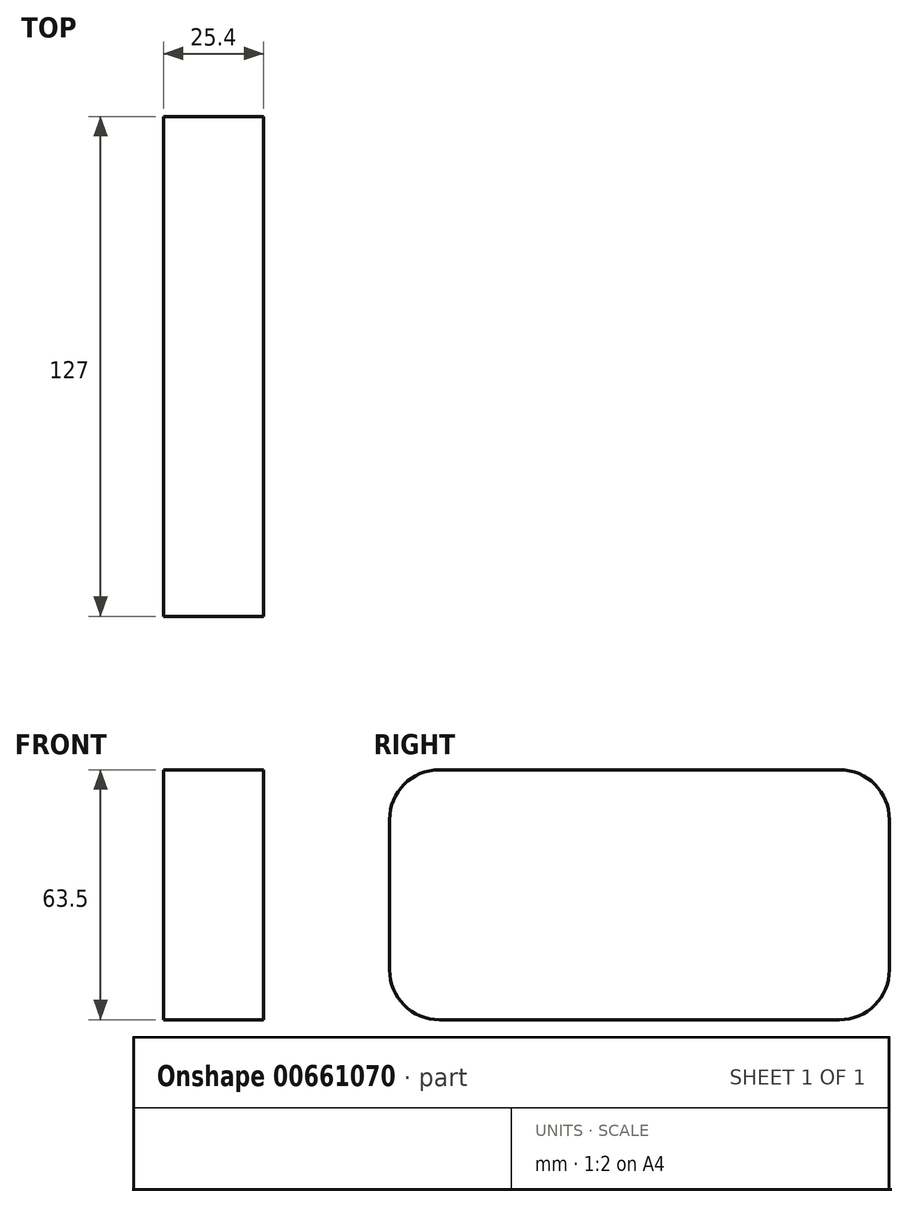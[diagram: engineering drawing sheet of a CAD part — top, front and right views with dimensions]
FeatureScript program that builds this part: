
annotation { "Feature Type Name" : "Feature", "Feature Type Description" : "" }
export const myFeature = defineFeature(function(context is Context, id is Id, definition is map)
    precondition{}
    {
        {
            var Q0;
            Q0=qCreatedBy(makeId("Right.planeOp"),FACE);
            var sketch = newSketch(context, id + "F0", { "sketchPlane" : qUnion([Q0])});
            skLineSegment(sketch, "E0.bottom", {"start": v(50.8, 31.75) * mm, "end": v(-50.8, 31.75) * mm});
            skLineSegment(sketch, "E0.top", {"start": v(50.8, -31.75) * mm, "end": v(-50.8, -31.75) * mm});
            skLineSegment(sketch, "E0.left", {"start": v(63.5, 19.05) * mm, "end": v(63.5, -19.05) * mm});
            skLineSegment(sketch, "E0.right", {"start": v(-63.5, 19.05) * mm, "end": v(-63.5, -19.05) * mm});
            skPoint(sketch, "E0.middle", {"position": v(0, 0) * mm});
            skPoint(sketch, "E1.visualSharp", {"position": v(-63.5, 31.75) * mm});
            skArc(sketch, "E1.filletArc", {"start": v(-50.8, 31.75) * mm, "mid": v(-59.78, 28.03) * mm, "end": v(-63.5, 19.05) * mm});
            skPoint(sketch, "E2.visualSharp", {"position": v(-63.5, -31.75) * mm});
            skArc(sketch, "E2.filletArc", {"start": v(-63.5, -19.05) * mm, "mid": v(-59.78, -28.03) * mm, "end": v(-50.8, -31.75) * mm});
            skPoint(sketch, "E3.visualSharp", {"position": v(63.5, -31.75) * mm});
            skArc(sketch, "E3.filletArc", {"start": v(50.8, -31.75) * mm, "mid": v(59.78, -28.03) * mm, "end": v(63.5, -19.05) * mm});
            skPoint(sketch, "E4.visualSharp", {"position": v(63.5, 31.75) * mm});
            skArc(sketch, "E4.filletArc", {"start": v(63.5, 19.05) * mm, "mid": v(59.78, 28.03) * mm, "end": v(50.8, 31.75) * mm});
            skSolve(sketch);
        }
        {
            var Q0;
            Q0=makeQuery(id+"F0.imprint","IMPRINT",FACE,{"disambiguationData":[TD([[makeQuery(id+"F0.imprint","IMPRINT",EDGE,{"derivedFrom":sQuery(id+"F0.wireOp",EDGE,"E0.bottom")}),1.0]])]});
            extrude(context, id + "F1", {"entities" : qUnion([Q0]), "endBound" : BoundingType.SYMMETRIC, "depth" : 25.4 * mm, "offsetDistance" : 25.4 * mm});
        }
    });
